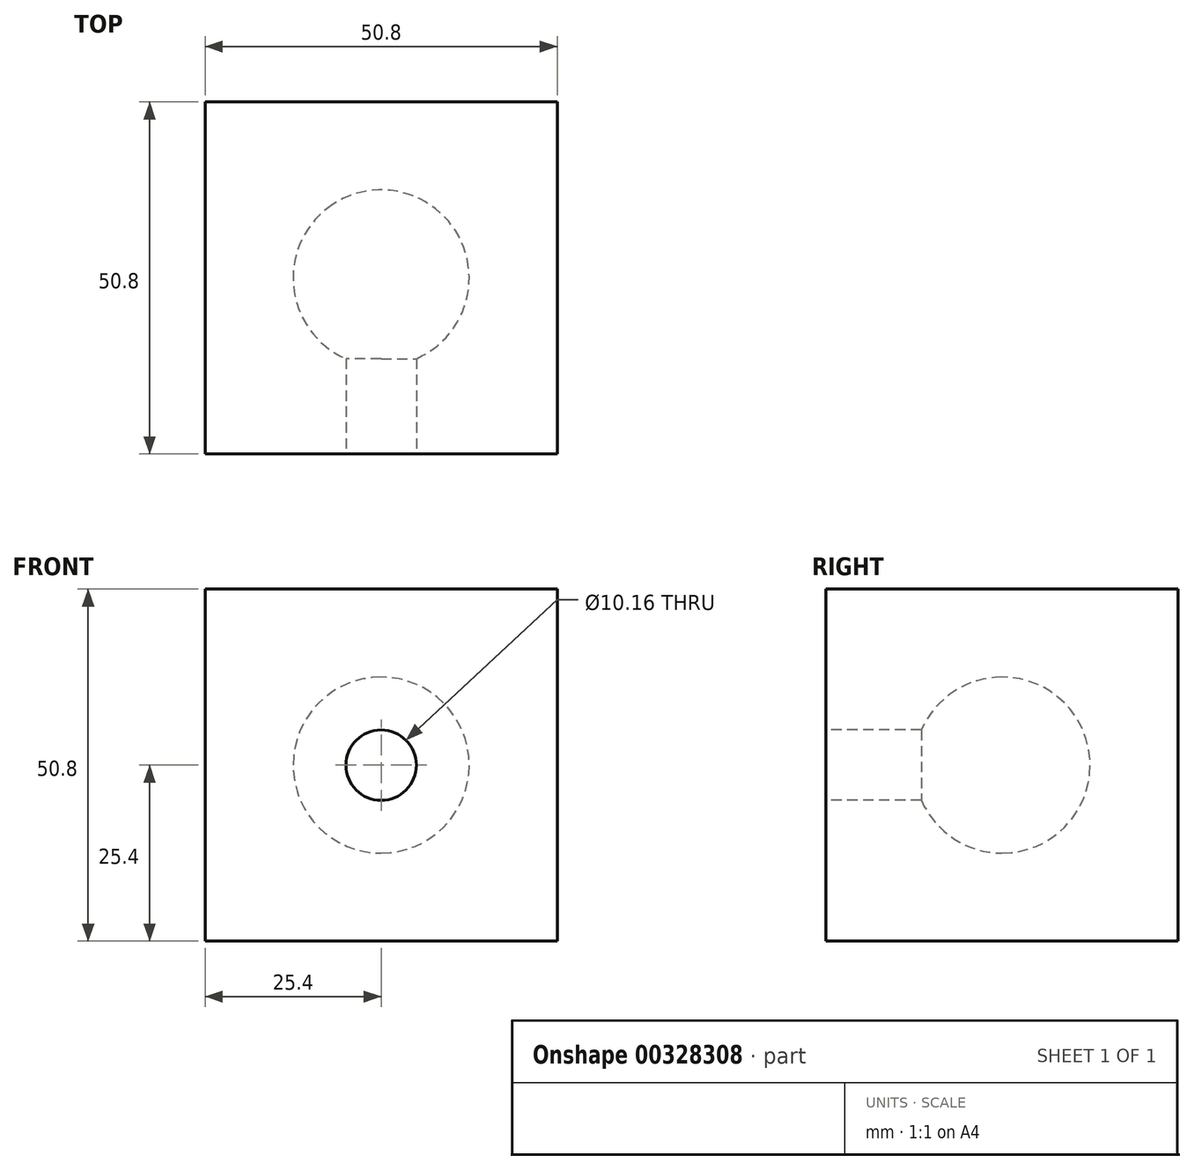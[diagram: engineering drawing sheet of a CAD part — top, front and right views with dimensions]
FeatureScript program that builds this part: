
annotation { "Feature Type Name" : "Feature", "Feature Type Description" : "" }
export const myFeature = defineFeature(function(context is Context, id is Id, definition is map)
    precondition{}
    {
        {
            var Q0;
            Q0=qCreatedBy(makeId("Front.planeOp"),FACE);
            var sketch = newSketch(context, id + "F0", { "sketchPlane" : qUnion([Q0])});
            skLineSegment(sketch, "E0.bottom", {"start": v(25.4, 25.4) * mm, "end": v(-25.4, 25.4) * mm});
            skLineSegment(sketch, "E0.top", {"start": v(25.4, -25.4) * mm, "end": v(-25.4, -25.4) * mm});
            skLineSegment(sketch, "E0.left", {"start": v(25.4, 25.4) * mm, "end": v(25.4, -25.4) * mm});
            skLineSegment(sketch, "E0.right", {"start": v(-25.4, 25.4) * mm, "end": v(-25.4, -25.4) * mm});
            skPoint(sketch, "E0.middle", {"position": v(0, 0) * mm});
            skSolve(sketch);
        }
        {
            var Q0;
            Q0 = qSketchRegion(id + "F0", true);
            extrude(context, id + "F1", {"entities" : qUnion([Q0]), "endBound" : BoundingType.SYMMETRIC, "depth" : 50.8 * mm});
        }
        {
            var Q0;
            Q0=qCreatedBy(makeId("Front.planeOp"),FACE);
            var sketch = newSketch(context, id + "F2", { "sketchPlane" : qUnion([Q0])});
            skArc(sketch, "E1", {"start": v(0, 12.7) * mm, "mid": v(-12.7, 0) * mm, "end": v(0, -12.7) * mm});
            skLineSegment(sketch, "E2", {"start": v(0, 12.7) * mm, "end": v(0, -12.7) * mm});
            skSolve(sketch);
        }
        {
            var Q0;
            Q0 = qSketchRegion(id + "F2", true);
            var Q1;
            Q1=sQuery(id+"F2.wireOp",EDGE,"E2");
            revolve(context, id + "F3", {"operationType" : NewBodyOperationType.REMOVE, "entities" : qUnion([Q0]), "axis" : qUnion([Q1]), "revolveType" : RevolveType.FULL, "oppositeDirection" : true});
        }
        {
            var Q0;
            Q0=makeQuery(id+"F1.opExtrude","CAP_FACE",FACE,{"disambiguationData":[OSD([sQuery(id+"F0.wireOp",EDGE,"E0.bottom"),sQuery(id+"F0.wireOp",EDGE,"E0.top"),sQuery(id+"F0.wireOp",EDGE,"E0.left"),sQuery(id+"F0.wireOp",EDGE,"E0.right")])],"isStart":false});
            var sketch = newSketch(context, id + "F4", { "sketchPlane" : qUnion([Q0])});
            skCircle(sketch, "E3", {"center": v(0, 0) * mm, "radius": 5.08 * mm});
            skSolve(sketch);
        }
        {
            var Q0;
            Q0 = qSketchRegion(id + "F4", true);
            extrude(context, id + "F5", {"entities" : qUnion([Q0]), "operationType" : NewBodyOperationType.REMOVE, "oppositeDirection" : true, "depth" : 25.4 * mm});
        }
    });
